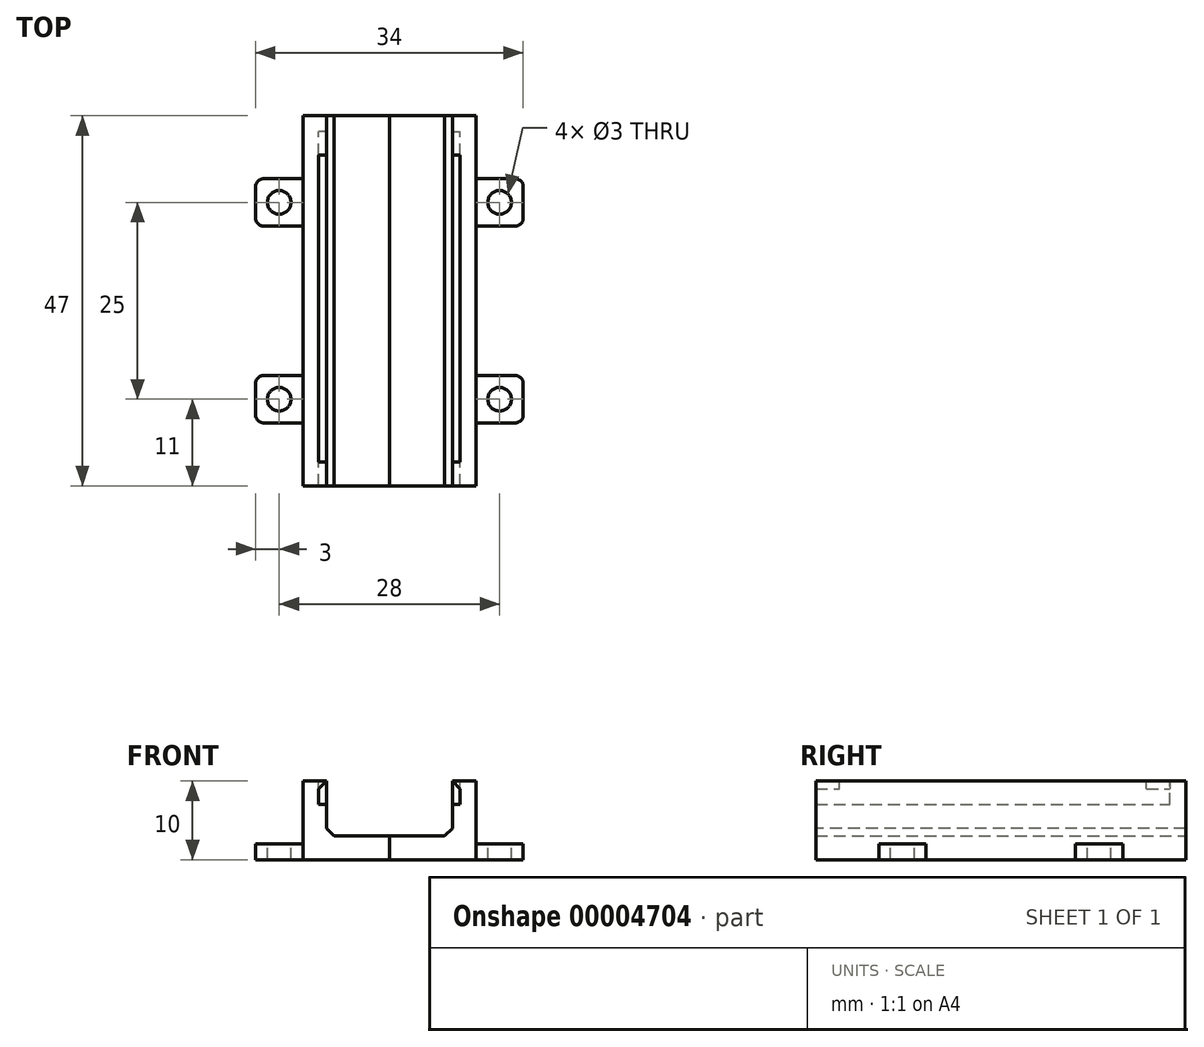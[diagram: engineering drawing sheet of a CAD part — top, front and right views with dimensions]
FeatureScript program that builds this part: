
annotation { "Feature Type Name" : "Feature", "Feature Type Description" : "" }
export const myFeature = defineFeature(function(context is Context, id is Id, definition is map)
    precondition{}
    {
        {
            var Q0;
            Q0=qCreatedBy(makeId("Front.planeOp"),FACE);
            var sketch = newSketch(context, id + "F0", { "sketchPlane" : qUnion([Q0])});
            skLineSegment(sketch, "E0", {"start": v(0, 0) * mm, "end": v(11, 0) * mm});
            skLineSegment(sketch, "E1", {"start": v(11, 0) * mm, "end": v(11, 10) * mm});
            skLineSegment(sketch, "E2", {"start": v(11, 10) * mm, "end": v(8, 10) * mm});
            skLineSegment(sketch, "E3", {"start": v(9, 7) * mm, "end": v(8, 7) * mm});
            skLineSegment(sketch, "E4", {"start": v(8, 7) * mm, "end": v(8, 3) * mm});
            skLineSegment(sketch, "E5", {"start": v(8, 3) * mm, "end": v(0, 3) * mm});
            skLineSegment(sketch, "E6", {"start": v(0, 3) * mm, "end": v(0, 0) * mm});
            skLineSegment(sketch, "E7", {"start": v(9, 9) * mm, "end": v(9, 7) * mm});
            skLineSegment(sketch, "E8", {"start": v(9, 9) * mm, "end": v(8, 10) * mm});
            skSolve(sketch);
        }
        {
            var Q0;
            Q0=makeQuery(id+"F0.imprint","IMPRINT",FACE,{"disambiguationData":[TD([[makeQuery(id+"F0.imprint","IMPRINT",EDGE,{"derivedFrom":sQuery(id+"F0.wireOp",EDGE,"E1")}),1.0]])]});
            extrude(context, id + "F1", {"entities" : qUnion([Q0]), "depth" : 47 * mm});
        }
        {
            var Q0;
            Q0=makeQuery(id+"F1.opExtrude","SWEPT_FACE",FACE,{"disambiguationData":[OSD([sQuery(id+"F0.wireOp",EDGE,"E1")])]});
            var sketch = newSketch(context, id + "F2", { "sketchPlane" : qUnion([Q0])});
            skLineSegment(sketch, "E9.bottom", {"start": v(-39, 2) * mm, "end": v(-33, 2) * mm});
            skLineSegment(sketch, "E9.top", {"start": v(-39, 0) * mm, "end": v(-33, 0) * mm});
            skLineSegment(sketch, "E9.left", {"start": v(-39, 2) * mm, "end": v(-39, 0) * mm});
            skLineSegment(sketch, "E9.right", {"start": v(-33, 2) * mm, "end": v(-33, 0) * mm});
            skLineSegment(sketch, "E10.bottom", {"start": v(-23.5, 10) * mm, "end": v(-23.5, 10) * mm});
            skLineSegment(sketch, "E10.top", {"start": v(-23.5, 0) * mm, "end": v(-23.5, 0) * mm});
            skLineSegment(sketch, "E10.left", {"start": v(-23.5, 10) * mm, "end": v(-23.5, 0) * mm, "construction": true});
            skLineSegment(sketch, "E10.right", {"start": v(-23.5, 10) * mm, "end": v(-23.5, 0) * mm, "construction": true});
            skLineSegment(sketch, "E11.0.MirrorCS", {"start": v(-8, 2) * mm, "end": v(-8, 0) * mm});
            skLineSegment(sketch, "E11.1.MirrorCS", {"start": v(-8, 0) * mm, "end": v(-14, 0) * mm});
            skLineSegment(sketch, "E11.2.MirrorCS", {"start": v(-8, 2) * mm, "end": v(-14, 2) * mm});
            skLineSegment(sketch, "E11.3.MirrorCS", {"start": v(-14, 2) * mm, "end": v(-14, 0) * mm});
            skSolve(sketch);
        }
        {
            var Q0;
            Q0=makeQuery(id+"F2.imprint","IMPRINT",FACE,{"disambiguationData":[TD([[makeQuery(id+"F2.imprint","IMPRINT",EDGE,{"derivedFrom":sQuery(id+"F2.wireOp",EDGE,"E9.bottom")}),-1.0]])]});
            var Q1;
            Q1=makeQuery(id+"F2.imprint","IMPRINT",FACE,{"disambiguationData":[TD([[makeQuery(id+"F2.imprint","IMPRINT",EDGE,{"derivedFrom":sQuery(id+"F2.wireOp",EDGE,"E11.0.MirrorCS")}),-1.0]])]});
            extrude(context, id + "F3", {"entities" : qUnion([Q0, Q1]), "operationType" : NewBodyOperationType.ADD, "depth" : 6 * mm});
        }
        {
            var Q0;
            Q0=makeQuery(id+"F3.opExtrude","CAP_EDGE",EDGE,{"disambiguationData":[OSD([sQuery(id+"F2.wireOp",EDGE,"E9.left")])],"isStart":false});
            var Q1;
            Q1=makeQuery(id+"F3.opExtrude","CAP_EDGE",EDGE,{"disambiguationData":[OSD([sQuery(id+"F2.wireOp",EDGE,"E9.right")])],"isStart":false});
            var Q2;
            Q2=makeQuery(id+"F3.opExtrude","CAP_EDGE",EDGE,{"disambiguationData":[OSD([sQuery(id+"F2.wireOp",EDGE,"E9.left")])],"isStart":true});
            var Q3;
            Q3=makeQuery(id+"F3.opExtrude","CAP_EDGE",EDGE,{"disambiguationData":[OSD([sQuery(id+"F2.wireOp",EDGE,"E9.right")])],"isStart":true});
            var Q4;
            Q4=makeQuery(id+"F3.opExtrude","CAP_EDGE",EDGE,{"disambiguationData":[OSD([sQuery(id+"F2.wireOp",EDGE,"E11.3.MirrorCS")])],"isStart":true});
            var Q5;
            Q5=makeQuery(id+"F3.opExtrude","CAP_EDGE",EDGE,{"disambiguationData":[OSD([sQuery(id+"F2.wireOp",EDGE,"E11.3.MirrorCS")])],"isStart":false});
            var Q6;
            Q6=makeQuery(id+"F3.opExtrude","CAP_EDGE",EDGE,{"disambiguationData":[OSD([sQuery(id+"F2.wireOp",EDGE,"E11.0.MirrorCS")])],"isStart":false});
            var Q7;
            Q7=makeQuery(id+"F3.opExtrude","CAP_EDGE",EDGE,{"disambiguationData":[OSD([sQuery(id+"F2.wireOp",EDGE,"E11.0.MirrorCS")])],"isStart":true});
            fillet(context, id + "F4", {"entities" : qUnion([Q0, Q1, Q2, Q3, Q4, Q5, Q6, Q7]), "radius" : 1 * mm, "tangentPropagation" : true, "allowEdgeOverflow" : false});
        }
        {
            var Q0;
            Q0=makeQuery(id+"F3.opExtrude","SWEPT_FACE",FACE,{"disambiguationData":[OSD([sQuery(id+"F2.wireOp",EDGE,"E9.bottom")])]});
            var sketch = newSketch(context, id + "F5", { "sketchPlane" : qUnion([Q0])});
            skCircle(sketch, "E12", {"center": v(14, -36) * mm, "radius": 1.5 * mm});
            skCircle(sketch, "E13", {"center": v(14, -11) * mm, "radius": 1.5 * mm});
            skSolve(sketch);
        }
        {
            var Q0;
            Q0 = qSketchRegion(id + "F5", true);
            extrude(context, id + "F6", {"entities" : qUnion([Q0]), "operationType" : NewBodyOperationType.REMOVE, "endBound" : BoundingType.THROUGH_ALL, "oppositeDirection" : true, "depth" : 25 * mm});
        }
        {
            var Q0;
            Q0=makeQuery(id+"F1.opExtrude","SWEPT_EDGE",EDGE,{"disambiguationData":[OSD([sQuery(id+"F0.wireOp",EDGE,"E4"),sQuery(id+"F0.wireOp",EDGE,"E5")])]});
            chamfer(context, id + "F7", {"entities" : qUnion([Q0]), "width" : 1 * mm, "tangentPropagation" : true});
        }
        {
            var Q0;
            Q0=makeQuery(id+"F1.opExtrude","SWEPT_FACE",FACE,{"disambiguationData":[OSD([sQuery(id+"F0.wireOp",EDGE,"E2")])]});
            var sketch = newSketch(context, id + "F8", { "sketchPlane" : qUnion([Q0])});
            skLineSegment(sketch, "E14.bottom", {"start": v(8, -44) * mm, "end": v(9, -44) * mm});
            skLineSegment(sketch, "E14.top", {"start": v(8, -5) * mm, "end": v(9, -5) * mm});
            skLineSegment(sketch, "E14.left", {"start": v(8, -44) * mm, "end": v(8, -5) * mm});
            skLineSegment(sketch, "E14.right", {"start": v(9, -44) * mm, "end": v(9, -5) * mm});
            skSolve(sketch);
        }
        {
            var Q0;
            Q0 = qSketchRegion(id + "F8", true);
            extrude(context, id + "F9", {"entities" : qUnion([Q0]), "operationType" : NewBodyOperationType.REMOVE, "oppositeDirection" : true, "depth" : 1 * mm});
        }
        {
            var Q0;
            Q0=makeQuery(id+"F9.boolean.opBoolean","MERGE",FACE,{"derivedFrom":[makeQuery(id+"F1.opExtrude","SWEPT_FACE",FACE,{"disambiguationData":[OSD([sQuery(id+"F0.wireOp",EDGE,"E7")])]}),makeQuery(id+"F9.opExtrude","SWEPT_FACE",FACE,{"disambiguationData":[OSD([sQuery(id+"F8.wireOp",EDGE,"88bea6ad-d598-4e63-be0c-82e83ab845ee"),sQuery(id+"F8.wireOp",EDGE,"ccd78b46-82a8-4c7c-873b-da9a81284193.0.MirrorCS")])]})]});
            var sketch = newSketch(context, id + "F10", { "sketchPlane" : qUnion([Q0])});
            skLineSegment(sketch, "E15.bottom", {"start": v(0, 7) * mm, "end": v(2, 7) * mm});
            skLineSegment(sketch, "E15.top", {"start": v(0, 10) * mm, "end": v(2, 10) * mm});
            skLineSegment(sketch, "E15.left", {"start": v(0, 7) * mm, "end": v(0, 10) * mm});
            skLineSegment(sketch, "E15.right", {"start": v(2, 7) * mm, "end": v(2, 10) * mm});
            skSolve(sketch);
        }
        {
            var Q0;
            Q0 = qSketchRegion(id + "F10", true);
            extrude(context, id + "F11", {"entities" : qUnion([Q0]), "operationType" : NewBodyOperationType.ADD, "depth" : 1 * mm});
        }
        {
            var Q0;
            Q0=makeQuery(id+"F1.opExtrude","SWEPT_BODY",BODY,{"disambiguationData":[OSD([sQuery(id+"F0.wireOp",EDGE,"E0"),sQuery(id+"F0.wireOp",EDGE,"E1"),sQuery(id+"F0.wireOp",EDGE,"E2"),sQuery(id+"F0.wireOp",EDGE,"3c63ed96-b616-4d6f-a9e6-944030ebc34d"),sQuery(id+"F0.wireOp",EDGE,"E3"),sQuery(id+"F0.wireOp",EDGE,"E4"),sQuery(id+"F0.wireOp",EDGE,"E5"),sQuery(id+"F0.wireOp",EDGE,"E6")])]});
            var Q1;
            Q1=makeQuery(id+"F1.opExtrude","SWEPT_FACE",FACE,{"disambiguationData":[OSD([sQuery(id+"F0.wireOp",EDGE,"E6")])]});
            mirror(context, id + "F12", {"entities" : qUnion([Q0]), "mirrorPlane" : qUnion([Q1])});
        }
    });
